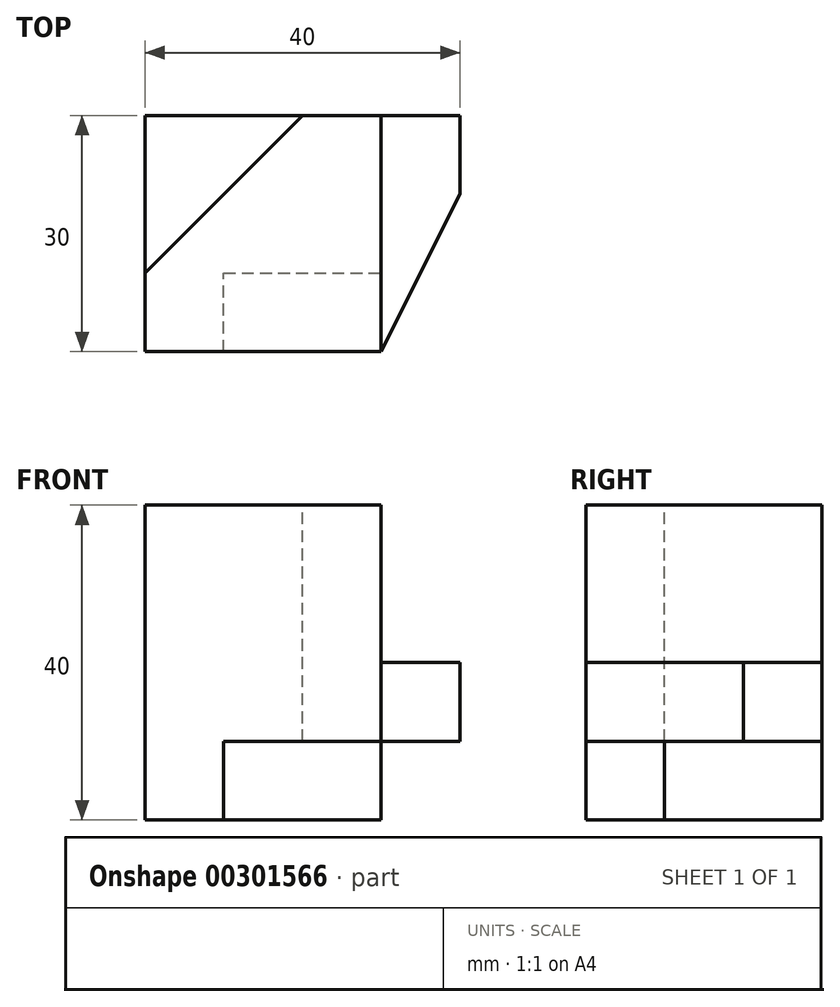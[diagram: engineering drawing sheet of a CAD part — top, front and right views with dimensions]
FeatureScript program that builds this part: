
annotation { "Feature Type Name" : "Feature", "Feature Type Description" : "" }
export const myFeature = defineFeature(function(context is Context, id is Id, definition is map)
    precondition{}
    {
        {
            var Q0;
            Q0=qCreatedBy(makeId("Top.planeOp"),FACE);
            var sketch = newSketch(context, id + "F0", { "sketchPlane" : qUnion([Q0])});
            skLineSegment(sketch, "E0.bottom", {"start": v(-20, 20) * mm, "end": v(20, 20) * mm});
            skLineSegment(sketch, "E0.top", {"start": v(-20, -20) * mm, "end": v(20, -20) * mm});
            skLineSegment(sketch, "E0.left", {"start": v(-20, 20) * mm, "end": v(-20, -20) * mm});
            skLineSegment(sketch, "E0.right", {"start": v(20, 20) * mm, "end": v(20, -20) * mm});
            skPoint(sketch, "E0.middle", {"position": v(0, 0) * mm});
            skSolve(sketch);
        }
        {
            var Q0;
            Q0=makeQuery(id+"F0.imprint","IMPRINT",FACE,{"disambiguationData":[TD([[makeQuery(id+"F0.imprint","IMPRINT",EDGE,{"derivedFrom":sQuery(id+"F0.wireOp",EDGE,"E0.bottom")}),-1.0]])]});
            extrude(context, id + "F1", {"entities" : qUnion([Q0]), "depth" : 30 * mm});
        }
        {
            var Q0;
            Q0=makeQuery(id+"F1.opExtrude","CAP_FACE",FACE,{"disambiguationData":[OSD([sQuery(id+"F0.wireOp",EDGE,"E0.bottom"),sQuery(id+"F0.wireOp",EDGE,"E0.top"),sQuery(id+"F0.wireOp",EDGE,"E0.left"),sQuery(id+"F0.wireOp",EDGE,"E0.right")])],"isStart":false});
            var sketch = newSketch(context, id + "F2", { "sketchPlane" : qUnion([Q0])});
            skLineSegment(sketch, "E1.bottom", {"start": v(20, 20) * mm, "end": v(10, 20) * mm});
            skLineSegment(sketch, "E1.top", {"start": v(20, 0) * mm, "end": v(10, 0) * mm});
            skLineSegment(sketch, "E1.left", {"start": v(20, 20) * mm, "end": v(20, 0) * mm});
            skLineSegment(sketch, "E1.right", {"start": v(10, 20) * mm, "end": v(10, 0) * mm});
            skLineSegment(sketch, "E2.bottom", {"start": v(20, -20) * mm, "end": v(10, -20) * mm});
            skLineSegment(sketch, "E2.top", {"start": v(20, -10) * mm, "end": v(10, -10) * mm});
            skLineSegment(sketch, "E2.left", {"start": v(20, -20) * mm, "end": v(20, -10) * mm});
            skLineSegment(sketch, "E2.right", {"start": v(10, -20) * mm, "end": v(10, -10) * mm});
            skSolve(sketch);
        }
        {
            var Q0;
            Q0=makeQuery(id+"F2.imprint","IMPRINT",FACE,{"disambiguationData":[TD([[makeQuery(id+"F2.imprint","IMPRINT",EDGE,{"derivedFrom":sQuery(id+"F2.wireOp",EDGE,"E1.bottom")}),-1.0]])]});
            var Q1;
            Q1=makeQuery(id+"F2.imprint","IMPRINT",FACE,{"disambiguationData":[TD([[makeQuery(id+"F2.imprint","IMPRINT",EDGE,{"derivedFrom":sQuery(id+"F2.wireOp",EDGE,"E2.bottom")}),1.0]])]});
            extrude(context, id + "F3", {"entities" : qUnion([Q0, Q1]), "operationType" : NewBodyOperationType.REMOVE, "oppositeDirection" : true, "depth" : 30 * mm});
        }
        {
            var Q0;
            Q0=makeQuery(id+"F1.opExtrude","SWEPT_FACE",FACE,{"disambiguationData":[OSD([sQuery(id+"F0.wireOp",EDGE,"E0.top")])]});
            var sketch = newSketch(context, id + "F4", { "sketchPlane" : qUnion([Q0])});
            skLineSegment(sketch, "E3.bottom", {"start": v(-10, 30) * mm, "end": v(10, 30) * mm});
            skLineSegment(sketch, "E3.top", {"start": v(-10, 20) * mm, "end": v(10, 20) * mm});
            skLineSegment(sketch, "E3.left", {"start": v(-10, 30) * mm, "end": v(-10, 20) * mm});
            skLineSegment(sketch, "E3.right", {"start": v(10, 30) * mm, "end": v(10, 20) * mm});
            skSolve(sketch);
        }
        {
            var Q0;
            Q0=makeQuery(id+"F4.imprint","IMPRINT",FACE,{"disambiguationData":[TD([[makeQuery(id+"F4.imprint","IMPRINT",EDGE,{"derivedFrom":sQuery(id+"F4.wireOp",EDGE,"E3.bottom")}),-1.0]])]});
            extrude(context, id + "F5", {"entities" : qUnion([Q0]), "operationType" : NewBodyOperationType.REMOVE, "oppositeDirection" : true, "depth" : 10 * mm});
        }
        {
            var Q0;
            Q0=makeQuery(id+"F5.boolean.opBoolean","MERGE",FACE,{"derivedFrom":[makeQuery(id+"F3.boolean.opBoolean","COPY",FACE,{"derivedFrom":makeQuery(id+"F3.opExtrude","SWEPT_FACE",FACE,{"disambiguationData":[OSD([sQuery(id+"F2.wireOp",EDGE,"E2.top")])]})}),makeQuery(id+"F5.opExtrude","CAP_FACE",FACE,{"disambiguationData":[OSD([sQuery(id+"F4.wireOp",EDGE,"E3.bottom"),sQuery(id+"F4.wireOp",EDGE,"E3.top"),sQuery(id+"F4.wireOp",EDGE,"E3.left"),sQuery(id+"F4.wireOp",EDGE,"E3.right")])],"isStart":false})]});
            var sketch = newSketch(context, id + "F6", { "sketchPlane" : qUnion([Q0])});
            skLineSegment(sketch, "E4", {"start": v(20, 30) * mm, "end": v(10, 30) * mm});
            skLineSegment(sketch, "E5", {"start": v(10, 30) * mm, "end": v(20, 10) * mm});
            skLineSegment(sketch, "E6", {"start": v(20, 10) * mm, "end": v(20, 30) * mm});
            skSolve(sketch);
        }
        {
            var Q0;
            Q0=makeQuery(id+"F6.imprint","IMPRINT",FACE,{"disambiguationData":[TD([[makeQuery(id+"F6.imprint","IMPRINT",EDGE,{"derivedFrom":sQuery(id+"F6.wireOp",EDGE,"E4")}),1.0]])]});
            extrude(context, id + "F7", {"entities" : qUnion([Q0]), "operationType" : NewBodyOperationType.REMOVE, "oppositeDirection" : true, "depth" : 10 * mm});
        }
        {
            var Q0;
            Q0=makeQuery(id+"F1.opExtrude","SWEPT_FACE",FACE,{"disambiguationData":[OSD([sQuery(id+"F0.wireOp",EDGE,"E0.bottom")])]});
            var sketch = newSketch(context, id + "F8", { "sketchPlane" : qUnion([Q0])});
            skLineSegment(sketch, "E7", {"start": v(20, 0) * mm, "end": v(0, 0) * mm});
            skLineSegment(sketch, "E8", {"start": v(0, 0) * mm, "end": v(20, 20) * mm});
            skLineSegment(sketch, "E9", {"start": v(20, 20) * mm, "end": v(20, 0) * mm});
            skSolve(sketch);
        }
        {
            var Q0;
            Q0=makeQuery(id+"F8.imprint","IMPRINT",FACE,{"disambiguationData":[TD([[makeQuery(id+"F8.imprint","IMPRINT",EDGE,{"derivedFrom":sQuery(id+"F8.wireOp",EDGE,"E7")}),-1.0]])]});
            extrude(context, id + "F9", {"entities" : qUnion([Q0]), "operationType" : NewBodyOperationType.REMOVE, "oppositeDirection" : true, "depth" : 30 * mm});
        }
        {
            var Q0;
            Q0=makeQuery(id+"F1.opExtrude","SWEPT_BODY",BODY,{"disambiguationData":[OSD([sQuery(id+"F0.wireOp",EDGE,"E0.bottom"),sQuery(id+"F0.wireOp",EDGE,"E0.top"),sQuery(id+"F0.wireOp",EDGE,"E0.left"),sQuery(id+"F0.wireOp",EDGE,"E0.right")])]});
            var Q1;
            Q1=makeQuery(id+"F1.opExtrude","CAP_EDGE",EDGE,{"disambiguationData":[OSD([sQuery(id+"F0.wireOp",EDGE,"E0.top")])],"isStart":true});
            var Q2;
            Q2=makeQuery(id+"F1.opExtrude","CAP_EDGE",EDGE,{"disambiguationData":[OSD([sQuery(id+"F0.wireOp",EDGE,"E0.top")])],"isStart":true});
            transform(context, id + "F10", {"entities" : qUnion([Q0]), "transformType" : TransformType.ROTATION, "transformAxis" : qUnion([Q2]), "angle" : 90 * degree, "makeCopy" : false});
        }
    });
